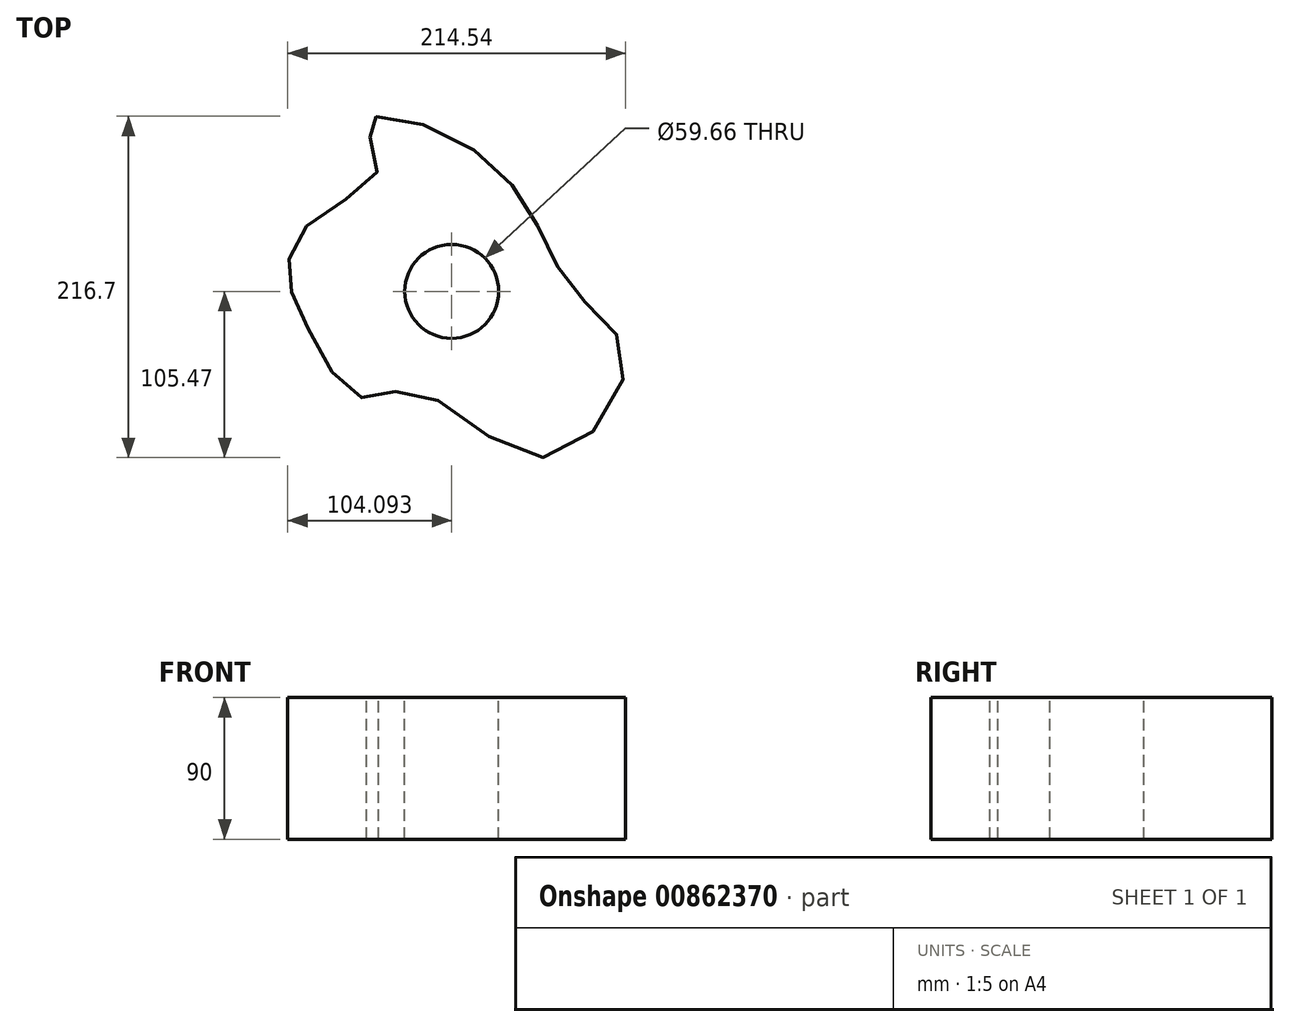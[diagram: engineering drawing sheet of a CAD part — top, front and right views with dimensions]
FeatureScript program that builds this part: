
annotation { "Feature Type Name" : "Feature", "Feature Type Description" : "" }
export const myFeature = defineFeature(function(context is Context, id is Id, definition is map)
    precondition{}
    {
        {
            var Q0;
            Q0=qCreatedBy(makeId("Top.planeOp"),FACE);
            var sketch = newSketch(context, id + "F0", { "sketchPlane" : qUnion([Q0])});
            skFitSpline(sketch, "E0", {"points": [v(-120.48, -23.45) * mm, v(-133.27, 12.74) * mm, v(-116.76, 45.58) * mm, v(-75.87, 78.3) * mm, v(-82.75, 107.78) * mm, v(-31.93, 99.62) * mm, v(20.98, 50.11) * mm, v(48.6, 0) * mm, v(81.2, -42.8) * mm, v(30.7, -105.4) * mm, v(-51.23, -63.53) * mm, v(-87.57, -67.28) * mm, v(-120.48, -23.45) * mm]});
            skSolve(sketch);
        }
        {
            var Q0;
            Q0=makeQuery(id+"F0.imprint","IMPRINT",FACE,{"disambiguationData":[TD([[makeQuery(id+"F0.imprint","IMPRINT",EDGE,{"derivedFrom":sQuery(id+"F0.wireOp",EDGE,"E0")}),-1.0]])]});
            extrude(context, id + "F1", {"entities" : qUnion([Q0]), "depth" : 25 * mm, "offsetDistance" : 25 * mm});
        }
        {
            var Q0;
            Q0=makeQuery(id+"F1.opExtrude","CAP_FACE",FACE,{"disambiguationData":[OSD([sQuery(id+"F0.wireOp",EDGE,"E0")])],"isStart":false});
            var sketch = newSketch(context, id + "F2", { "sketchPlane" : qUnion([Q0])});
            skCircle(sketch, "E1", {"center": v(-29.18, 0) * mm, "radius": 29.83 * mm});
            skSolve(sketch);
        }
        {
            var Q0;
            Q0=makeQuery(id+"F2.imprint","IMPRINT",FACE,{"disambiguationData":[TD([[makeQuery(id+"F2.imprint","IMPRINT",EDGE,{"derivedFrom":sQuery(id+"F2.wireOp",EDGE,"E1")}),1.0]])]});
            extrude(context, id + "F3", {"entities" : qUnion([Q0]), "operationType" : NewBodyOperationType.REMOVE, "oppositeDirection" : true, "depth" : 25 * mm, "offsetDistance" : 25 * mm});
        }
        {
            var Q0;
            Q0=makeQuery(id+"F1.opExtrude","CAP_FACE",FACE,{"disambiguationData":[OSD([sQuery(id+"F0.wireOp",EDGE,"E0")])],"isStart":false});
            extrude(context, id + "F4", {"entities" : qUnion([Q0]), "operationType" : NewBodyOperationType.ADD, "depth" : 65 * mm, "offsetDistance" : 25 * mm});
        }
    });
